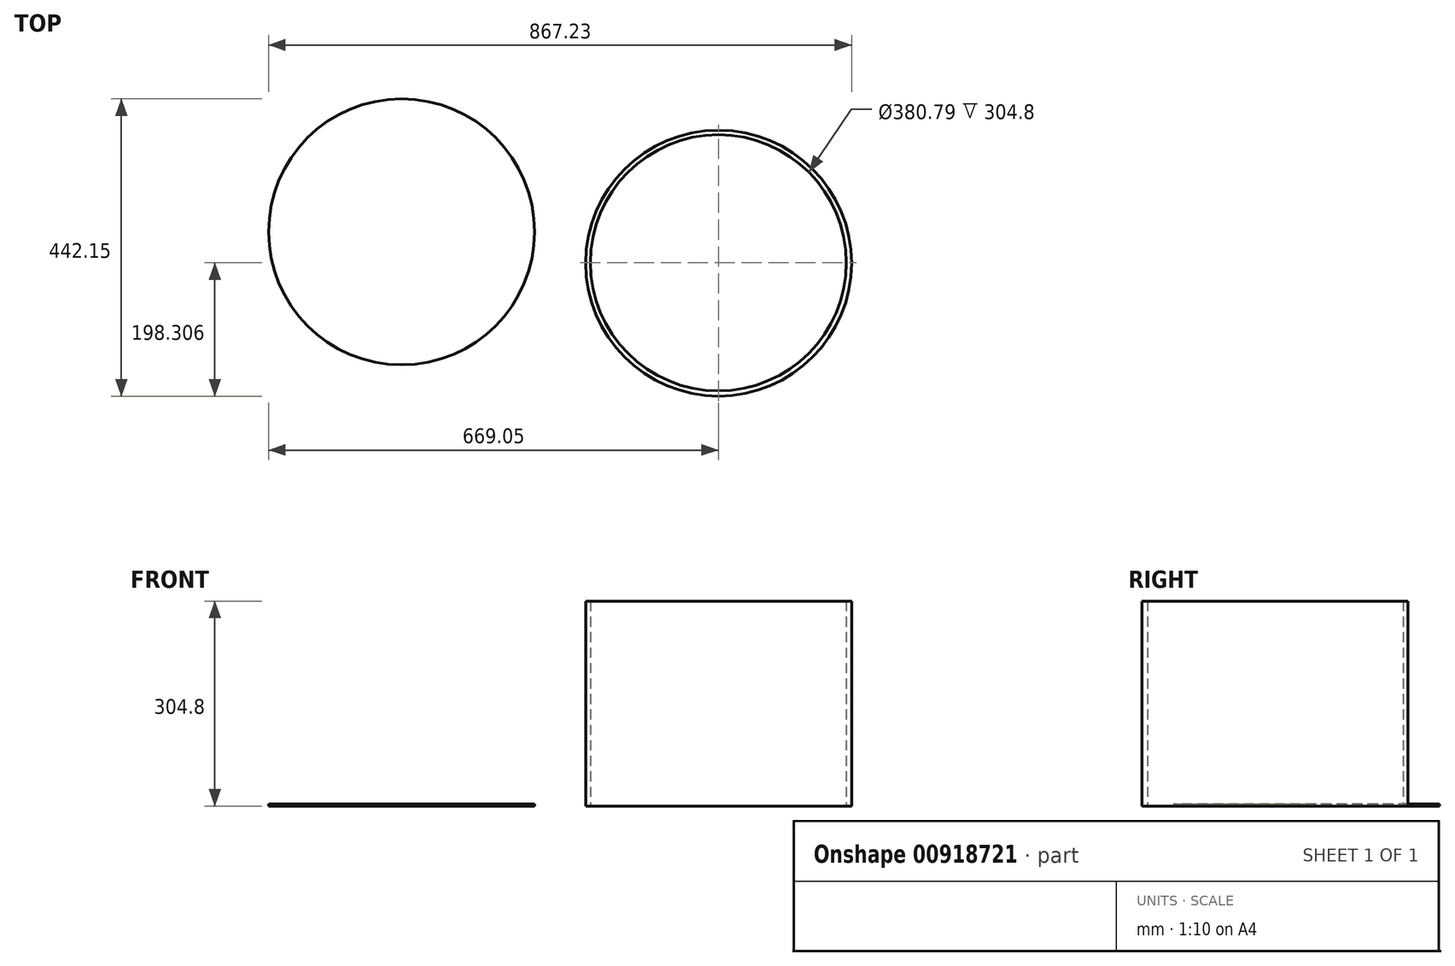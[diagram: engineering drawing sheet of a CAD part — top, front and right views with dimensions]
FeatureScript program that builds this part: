
annotation { "Feature Type Name" : "Feature", "Feature Type Description" : "" }
export const myFeature = defineFeature(function(context is Context, id is Id, definition is map)
    precondition{}
    {
        {
            var Q0;
            Q0=qCreatedBy(makeId("Top.planeOp"),FACE);
            var sketch = newSketch(context, id + "F0", { "sketchPlane" : qUnion([Q0])});
            skCircle(sketch, "E0", {"center": v(0, 0) * mm, "radius": 197.8 * mm});
            skSolve(sketch);
        }
        {
            var Q0;
            Q0 = qSketchRegion(id + "F0", true);
            extrude(context, id + "F1", {"entities" : qUnion([Q0]), "depth" : 3.17 * mm, "offsetDistance" : 25.4 * mm});
        }
        {
            var Q0;
            Q0=qCreatedBy(makeId("Top.planeOp"),FACE);
            var sketch = newSketch(context, id + "F2", { "sketchPlane" : qUnion([Q0])});
            skCircle(sketch, "E1", {"center": v(471.63, -46.55) * mm, "radius": 197.8 * mm});
            skSolve(sketch);
        }
        {
            var Q0;
            Q0=makeQuery(id+"F2.imprint","IMPRINT",FACE,{"disambiguationData":[TD([[makeQuery(id+"F2.imprint","IMPRINT",EDGE,{"derivedFrom":sQuery(id+"F2.wireOp",EDGE,"E1")}),1.0]])]});
            var sketch = newSketch(context, id + "F3", { "sketchPlane" : qUnion([Q0])});
            skCircle(sketch, "E2", {"center": v(471.25, -46.04) * mm, "radius": 190.4 * mm});
            skSolve(sketch);
        }
        {
            var Q0;
            Q0=makeQuery(id+"F3.imprint","IMPRINT",FACE,{"disambiguationData":[TD([[makeQuery(id+"F3.imprint","IMPRINT",EDGE,{"derivedFrom":sQuery(id+"F3.wireOp",EDGE,"E2")}),-1.0]])]});
            extrude(context, id + "F4", {"entities" : qUnion([Q0]), "depth" : 304.8 * mm, "offsetDistance" : 25.4 * mm});
        }
    });
